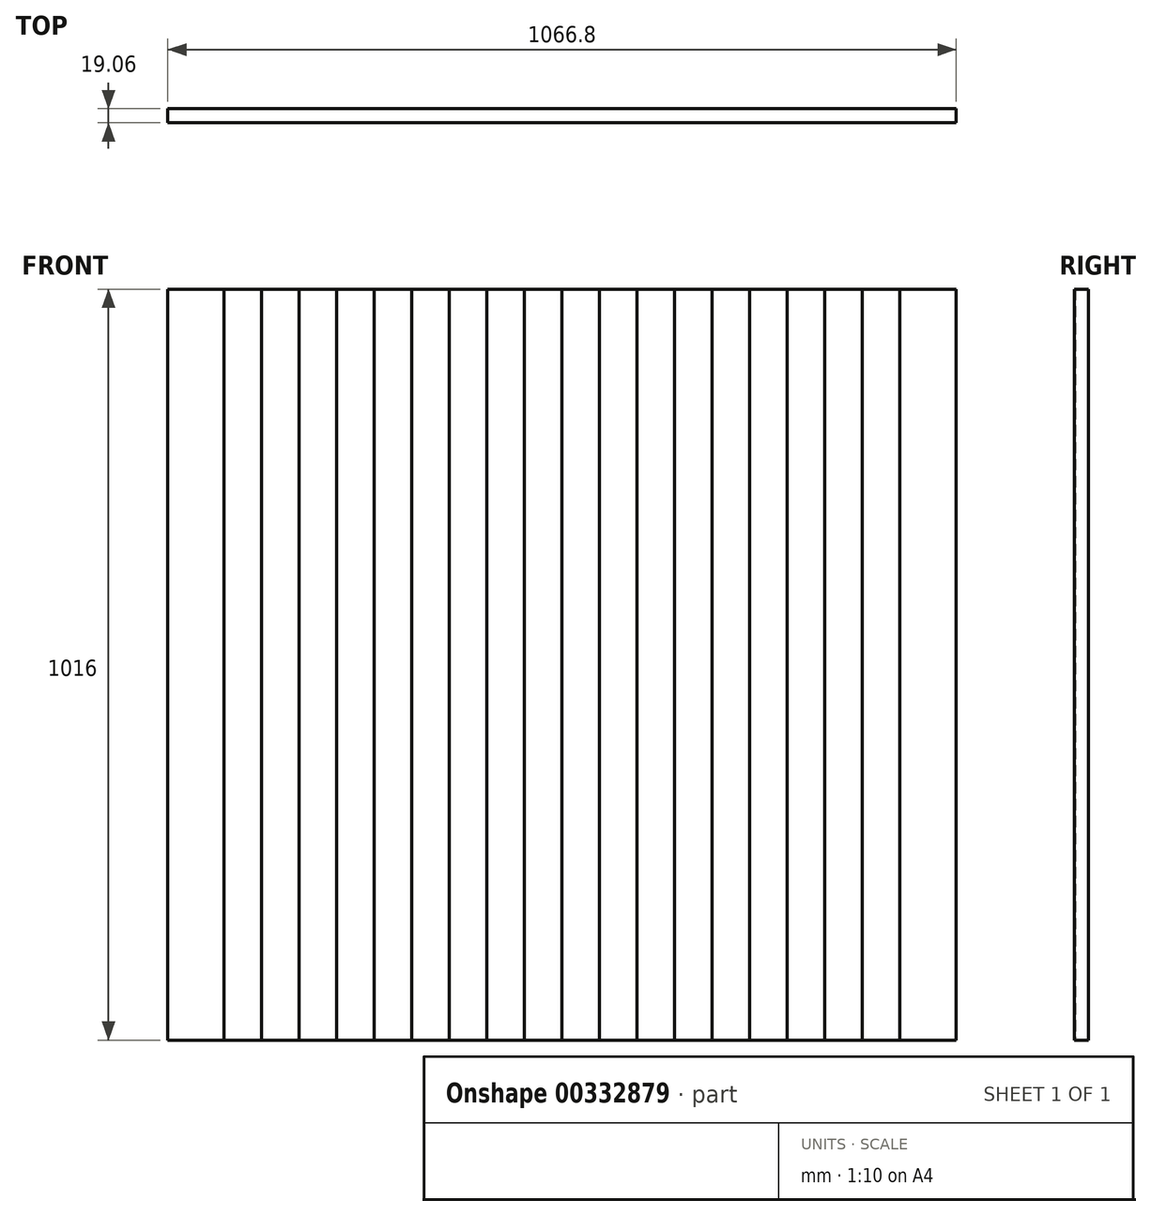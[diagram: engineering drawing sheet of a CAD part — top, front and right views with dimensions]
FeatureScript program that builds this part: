
annotation { "Feature Type Name" : "Feature", "Feature Type Description" : "" }
export const myFeature = defineFeature(function(context is Context, id is Id, definition is map)
    precondition{}
    {
        {
            var Q0;
            Q0=qCreatedBy(makeId("Top.planeOp"),FACE);
            var sketch = newSketch(context, id + "F0", { "sketchPlane" : qUnion([Q0])});
            skLineSegment(sketch, "E0.bottom", {"start": v(533.4, -9.53) * mm, "end": v(458.22, -9.53) * mm});
            skLineSegment(sketch, "E0.top", {"start": v(533.4, 9.53) * mm, "end": v(-533.4, 9.53) * mm});
            skLineSegment(sketch, "E0.left", {"start": v(533.4, 9.53) * mm, "end": v(533.4, -9.53) * mm});
            skLineSegment(sketch, "E0.right", {"start": v(-533.4, 9.53) * mm, "end": v(-533.4, -9.53) * mm});
            skPoint(sketch, "E0.middle", {"position": v(0, 0) * mm});
            skArc(sketch, "E1", {"start": v(-509.02, -9.53) * mm, "mid": v(-508.3, -9.23) * mm, "end": v(-508, -8.5) * mm});
            skArc(sketch, "E2", {"start": v(-508, -8.5) * mm, "mid": v(-507.7, -9.23) * mm, "end": v(-506.98, -9.52) * mm});
            skArc(sketch, "E3.1.0.0", {"start": v(-458.22, -9.53) * mm, "mid": v(-457.5, -9.23) * mm, "end": v(-457.2, -8.5) * mm});
            skArc(sketch, "E3.1.0.1", {"start": v(-457.2, -8.5) * mm, "mid": v(-456.9, -9.23) * mm, "end": v(-456.18, -9.52) * mm});
            skArc(sketch, "E3.2.0.0", {"start": v(-407.42, -9.53) * mm, "mid": v(-406.7, -9.23) * mm, "end": v(-406.4, -8.5) * mm});
            skArc(sketch, "E3.2.0.1", {"start": v(-406.4, -8.5) * mm, "mid": v(-406.1, -9.23) * mm, "end": v(-405.38, -9.52) * mm});
            skArc(sketch, "E3.3.0.0", {"start": v(-356.62, -9.53) * mm, "mid": v(-355.9, -9.23) * mm, "end": v(-355.6, -8.5) * mm});
            skArc(sketch, "E3.3.0.1", {"start": v(-355.6, -8.5) * mm, "mid": v(-355.3, -9.23) * mm, "end": v(-354.58, -9.52) * mm});
            skArc(sketch, "E3.4.0.0", {"start": v(-305.82, -9.53) * mm, "mid": v(-305.1, -9.23) * mm, "end": v(-304.8, -8.5) * mm});
            skArc(sketch, "E3.4.0.1", {"start": v(-304.8, -8.5) * mm, "mid": v(-304.5, -9.23) * mm, "end": v(-303.78, -9.52) * mm});
            skArc(sketch, "E3.5.0.0", {"start": v(-255.02, -9.53) * mm, "mid": v(-254.3, -9.23) * mm, "end": v(-254, -8.5) * mm});
            skArc(sketch, "E3.5.0.1", {"start": v(-254, -8.5) * mm, "mid": v(-253.7, -9.23) * mm, "end": v(-252.98, -9.52) * mm});
            skArc(sketch, "E3.6.0.0", {"start": v(-204.22, -9.53) * mm, "mid": v(-203.5, -9.23) * mm, "end": v(-203.2, -8.5) * mm});
            skArc(sketch, "E3.6.0.1", {"start": v(-203.2, -8.5) * mm, "mid": v(-202.9, -9.23) * mm, "end": v(-202.18, -9.52) * mm});
            skArc(sketch, "E3.7.0.0", {"start": v(-153.42, -9.53) * mm, "mid": v(-152.7, -9.23) * mm, "end": v(-152.4, -8.5) * mm});
            skArc(sketch, "E3.7.0.1", {"start": v(-152.4, -8.5) * mm, "mid": v(-152.1, -9.23) * mm, "end": v(-151.38, -9.52) * mm});
            skArc(sketch, "E3.8.0.0", {"start": v(-102.62, -9.53) * mm, "mid": v(-101.9, -9.23) * mm, "end": v(-101.6, -8.5) * mm});
            skArc(sketch, "E3.8.0.1", {"start": v(-101.6, -8.5) * mm, "mid": v(-101.3, -9.23) * mm, "end": v(-100.58, -9.52) * mm});
            skArc(sketch, "E3.9.0.0", {"start": v(-51.82, -9.53) * mm, "mid": v(-51.1, -9.23) * mm, "end": v(-50.8, -8.5) * mm});
            skArc(sketch, "E3.9.0.1", {"start": v(-50.8, -8.5) * mm, "mid": v(-50.5, -9.23) * mm, "end": v(-49.78, -9.52) * mm});
            skArc(sketch, "E3.10.0.0", {"start": v(-1.02, -9.53) * mm, "mid": v(-0.3, -9.23) * mm, "end": v(0, -8.5) * mm});
            skArc(sketch, "E3.10.0.1", {"start": v(0, -8.5) * mm, "mid": v(0.3, -9.23) * mm, "end": v(1.02, -9.52) * mm});
            skArc(sketch, "E3.11.0.0", {"start": v(49.78, -9.53) * mm, "mid": v(50.5, -9.23) * mm, "end": v(50.8, -8.5) * mm});
            skArc(sketch, "E3.11.0.1", {"start": v(50.8, -8.5) * mm, "mid": v(51.1, -9.23) * mm, "end": v(51.82, -9.52) * mm});
            skArc(sketch, "E3.12.0.0", {"start": v(100.58, -9.53) * mm, "mid": v(101.3, -9.23) * mm, "end": v(101.6, -8.5) * mm});
            skArc(sketch, "E3.12.0.1", {"start": v(101.6, -8.5) * mm, "mid": v(101.9, -9.23) * mm, "end": v(102.62, -9.52) * mm});
            skArc(sketch, "E3.13.0.0", {"start": v(151.38, -9.53) * mm, "mid": v(152.1, -9.23) * mm, "end": v(152.4, -8.5) * mm});
            skArc(sketch, "E3.13.0.1", {"start": v(152.4, -8.5) * mm, "mid": v(152.7, -9.23) * mm, "end": v(153.42, -9.52) * mm});
            skArc(sketch, "E3.14.0.0", {"start": v(202.18, -9.53) * mm, "mid": v(202.9, -9.23) * mm, "end": v(203.2, -8.5) * mm});
            skArc(sketch, "E3.14.0.1", {"start": v(203.2, -8.5) * mm, "mid": v(203.5, -9.23) * mm, "end": v(204.22, -9.52) * mm});
            skArc(sketch, "E3.15.0.0", {"start": v(252.98, -9.53) * mm, "mid": v(253.7, -9.23) * mm, "end": v(254, -8.5) * mm});
            skArc(sketch, "E3.15.0.1", {"start": v(254, -8.5) * mm, "mid": v(254.3, -9.23) * mm, "end": v(255.02, -9.52) * mm});
            skArc(sketch, "E3.16.0.0", {"start": v(303.78, -9.53) * mm, "mid": v(304.5, -9.23) * mm, "end": v(304.8, -8.5) * mm});
            skArc(sketch, "E3.16.0.1", {"start": v(304.8, -8.5) * mm, "mid": v(305.1, -9.23) * mm, "end": v(305.82, -9.52) * mm});
            skArc(sketch, "E3.17.0.0", {"start": v(354.58, -9.53) * mm, "mid": v(355.3, -9.23) * mm, "end": v(355.6, -8.5) * mm});
            skArc(sketch, "E3.17.0.1", {"start": v(355.6, -8.5) * mm, "mid": v(355.9, -9.23) * mm, "end": v(356.62, -9.52) * mm});
            skArc(sketch, "E3.18.0.0", {"start": v(405.38, -9.53) * mm, "mid": v(406.1, -9.23) * mm, "end": v(406.4, -8.5) * mm});
            skArc(sketch, "E3.18.0.1", {"start": v(406.4, -8.5) * mm, "mid": v(406.7, -9.23) * mm, "end": v(407.42, -9.52) * mm});
            skArc(sketch, "E3.19.0.0", {"start": v(456.18, -9.53) * mm, "mid": v(456.9, -9.23) * mm, "end": v(457.2, -8.5) * mm});
            skArc(sketch, "E3.19.0.1", {"start": v(457.2, -8.5) * mm, "mid": v(457.5, -9.23) * mm, "end": v(458.22, -9.52) * mm});
            skLineSegment(sketch, "E3.direction1", {"start": v(-506.98, -9.53) * mm, "end": v(-458.22, -9.53) * mm, "construction": true});
            skLineSegment(sketch, "E4.trimOffspring", {"start": v(-458.22, -9.53) * mm, "end": v(-533.4, -9.53) * mm});
            skLineSegment(sketch, "E5.trimOffspring", {"start": v(-407.42, -9.53) * mm, "end": v(-456.18, -9.53) * mm});
            skLineSegment(sketch, "E6.trimOffspring", {"start": v(-356.62, -9.53) * mm, "end": v(-405.38, -9.53) * mm});
            skLineSegment(sketch, "E7.trimOffspring", {"start": v(-305.82, -9.53) * mm, "end": v(-354.58, -9.53) * mm});
            skLineSegment(sketch, "E8.trimOffspring", {"start": v(-255.02, -9.53) * mm, "end": v(-303.78, -9.53) * mm});
            skLineSegment(sketch, "E9.trimOffspring", {"start": v(-204.22, -9.53) * mm, "end": v(-252.98, -9.53) * mm});
            skLineSegment(sketch, "E10.trimOffspring", {"start": v(-153.42, -9.53) * mm, "end": v(-202.18, -9.53) * mm});
            skLineSegment(sketch, "E11.trimOffspring", {"start": v(-102.62, -9.53) * mm, "end": v(-151.38, -9.53) * mm});
            skLineSegment(sketch, "E12.trimOffspring", {"start": v(-51.82, -9.53) * mm, "end": v(-100.58, -9.53) * mm});
            skLineSegment(sketch, "E13.trimOffspring", {"start": v(-1.02, -9.53) * mm, "end": v(-49.78, -9.53) * mm});
            skLineSegment(sketch, "E14.trimOffspring", {"start": v(49.78, -9.53) * mm, "end": v(1.02, -9.53) * mm});
            skLineSegment(sketch, "E15.trimOffspring", {"start": v(100.58, -9.53) * mm, "end": v(51.82, -9.53) * mm});
            skLineSegment(sketch, "E16.trimOffspring", {"start": v(151.38, -9.53) * mm, "end": v(102.62, -9.53) * mm});
            skLineSegment(sketch, "E17.trimOffspring", {"start": v(202.18, -9.53) * mm, "end": v(153.42, -9.53) * mm});
            skLineSegment(sketch, "E18.trimOffspring", {"start": v(252.98, -9.53) * mm, "end": v(204.22, -9.53) * mm});
            skLineSegment(sketch, "E19.trimOffspring", {"start": v(303.78, -9.53) * mm, "end": v(255.02, -9.53) * mm});
            skLineSegment(sketch, "E20.trimOffspring", {"start": v(354.58, -9.53) * mm, "end": v(305.82, -9.53) * mm});
            skLineSegment(sketch, "E21.trimOffspring", {"start": v(405.38, -9.53) * mm, "end": v(356.62, -9.53) * mm});
            skLineSegment(sketch, "E22.trimOffspring", {"start": v(456.18, -9.53) * mm, "end": v(407.42, -9.53) * mm});
            skArc(sketch, "E23.0.20.0", {"start": v(506.98, -9.53) * mm, "mid": v(507.7, -9.23) * mm, "end": v(508, -8.5) * mm});
            skArc(sketch, "E23.4.20.0", {"start": v(508, -8.5) * mm, "mid": v(508.3, -9.23) * mm, "end": v(509.02, -9.52) * mm});
            skArc(sketch, "E23.0.21.0", {"start": v(557.78, -9.53) * mm, "mid": v(558.5, -9.23) * mm, "end": v(558.8, -8.5) * mm});
            skArc(sketch, "E23.4.21.0", {"start": v(558.8, -8.5) * mm, "mid": v(559.1, -9.23) * mm, "end": v(559.82, -9.52) * mm});
            skArc(sketch, "E23.0.22.0", {"start": v(608.58, -9.53) * mm, "mid": v(609.3, -9.23) * mm, "end": v(609.6, -8.5) * mm});
            skArc(sketch, "E23.4.22.0", {"start": v(609.6, -8.5) * mm, "mid": v(609.9, -9.23) * mm, "end": v(610.62, -9.52) * mm});
            skArc(sketch, "E23.0.23.0", {"start": v(659.38, -9.53) * mm, "mid": v(660.1, -9.23) * mm, "end": v(660.4, -8.5) * mm});
            skArc(sketch, "E23.4.23.0", {"start": v(660.4, -8.5) * mm, "mid": v(660.7, -9.23) * mm, "end": v(661.42, -9.52) * mm});
            skArc(sketch, "E23.0.24.0", {"start": v(710.18, -9.53) * mm, "mid": v(710.9, -9.23) * mm, "end": v(711.2, -8.5) * mm});
            skArc(sketch, "E23.4.24.0", {"start": v(711.2, -8.5) * mm, "mid": v(711.5, -9.23) * mm, "end": v(712.22, -9.52) * mm});
            skArc(sketch, "E23.0.25.0", {"start": v(760.98, -9.53) * mm, "mid": v(761.7, -9.23) * mm, "end": v(762, -8.5) * mm});
            skArc(sketch, "E23.4.25.0", {"start": v(762, -8.5) * mm, "mid": v(762.3, -9.23) * mm, "end": v(763.02, -9.52) * mm});
            skArc(sketch, "E23.0.26.0", {"start": v(811.78, -9.53) * mm, "mid": v(812.5, -9.23) * mm, "end": v(812.8, -8.5) * mm});
            skArc(sketch, "E23.4.26.0", {"start": v(812.8, -8.5) * mm, "mid": v(813.1, -9.23) * mm, "end": v(813.82, -9.52) * mm});
            skArc(sketch, "E23.0.27.0", {"start": v(862.58, -9.53) * mm, "mid": v(863.3, -9.23) * mm, "end": v(863.6, -8.5) * mm});
            skArc(sketch, "E23.4.27.0", {"start": v(863.6, -8.5) * mm, "mid": v(863.9, -9.23) * mm, "end": v(864.62, -9.52) * mm});
            skArc(sketch, "E23.0.28.0", {"start": v(913.38, -9.53) * mm, "mid": v(914.1, -9.23) * mm, "end": v(914.4, -8.5) * mm});
            skArc(sketch, "E23.4.28.0", {"start": v(914.4, -8.5) * mm, "mid": v(914.7, -9.23) * mm, "end": v(915.42, -9.52) * mm});
            skArc(sketch, "E23.0.29.0", {"start": v(964.18, -9.53) * mm, "mid": v(964.9, -9.23) * mm, "end": v(965.2, -8.5) * mm});
            skArc(sketch, "E23.4.29.0", {"start": v(965.2, -8.5) * mm, "mid": v(965.5, -9.23) * mm, "end": v(966.22, -9.52) * mm});
            skArc(sketch, "E23.0.30.0", {"start": v(1014.98, -9.53) * mm, "mid": v(1015.7, -9.23) * mm, "end": v(1016, -8.5) * mm});
            skArc(sketch, "E23.4.30.0", {"start": v(1016, -8.5) * mm, "mid": v(1016.3, -9.23) * mm, "end": v(1017.02, -9.52) * mm});
            skArc(sketch, "E23.0.31.0", {"start": v(1065.78, -9.53) * mm, "mid": v(1066.5, -9.23) * mm, "end": v(1066.8, -8.5) * mm});
            skArc(sketch, "E23.4.31.0", {"start": v(1066.8, -8.5) * mm, "mid": v(1067.1, -9.23) * mm, "end": v(1067.82, -9.52) * mm});
            skArc(sketch, "E23.0.32.0", {"start": v(1116.58, -9.53) * mm, "mid": v(1117.3, -9.23) * mm, "end": v(1117.6, -8.5) * mm});
            skArc(sketch, "E23.4.32.0", {"start": v(1117.6, -8.5) * mm, "mid": v(1117.9, -9.23) * mm, "end": v(1118.62, -9.52) * mm});
            skArc(sketch, "E23.0.33.0", {"start": v(1167.38, -9.53) * mm, "mid": v(1168.1, -9.23) * mm, "end": v(1168.4, -8.5) * mm});
            skArc(sketch, "E23.4.33.0", {"start": v(1168.4, -8.5) * mm, "mid": v(1168.7, -9.23) * mm, "end": v(1169.42, -9.52) * mm});
            skArc(sketch, "E23.0.34.0", {"start": v(1218.18, -9.53) * mm, "mid": v(1218.9, -9.23) * mm, "end": v(1219.2, -8.5) * mm});
            skArc(sketch, "E23.4.34.0", {"start": v(1219.2, -8.5) * mm, "mid": v(1219.5, -9.23) * mm, "end": v(1220.22, -9.52) * mm});
            skArc(sketch, "E23.0.35.0", {"start": v(1268.98, -9.53) * mm, "mid": v(1269.7, -9.23) * mm, "end": v(1270, -8.5) * mm});
            skArc(sketch, "E23.4.35.0", {"start": v(1270, -8.5) * mm, "mid": v(1270.3, -9.23) * mm, "end": v(1271.02, -9.52) * mm});
            skArc(sketch, "E23.0.36.0", {"start": v(1319.78, -9.53) * mm, "mid": v(1320.5, -9.23) * mm, "end": v(1320.8, -8.5) * mm});
            skArc(sketch, "E23.4.36.0", {"start": v(1320.8, -8.5) * mm, "mid": v(1321.1, -9.23) * mm, "end": v(1321.82, -9.52) * mm});
            skArc(sketch, "E23.0.37.0", {"start": v(1370.58, -9.53) * mm, "mid": v(1371.3, -9.23) * mm, "end": v(1371.6, -8.5) * mm});
            skArc(sketch, "E23.4.37.0", {"start": v(1371.6, -8.5) * mm, "mid": v(1371.9, -9.23) * mm, "end": v(1372.62, -9.52) * mm});
            skArc(sketch, "E23.0.38.0", {"start": v(1421.38, -9.53) * mm, "mid": v(1422.1, -9.23) * mm, "end": v(1422.4, -8.5) * mm});
            skArc(sketch, "E23.4.38.0", {"start": v(1422.4, -8.5) * mm, "mid": v(1422.7, -9.23) * mm, "end": v(1423.42, -9.52) * mm});
            skArc(sketch, "E23.0.39.0", {"start": v(1472.18, -9.53) * mm, "mid": v(1472.9, -9.23) * mm, "end": v(1473.2, -8.5) * mm});
            skArc(sketch, "E23.4.39.0", {"start": v(1473.2, -8.5) * mm, "mid": v(1473.5, -9.23) * mm, "end": v(1474.22, -9.52) * mm});
            skSolve(sketch);
        }
        {
            var Q0;
            Q0 = qSketchRegion(id + "F0", true);
            extrude(context, id + "F1", {"entities" : qUnion([Q0]), "depth" : 1016 * mm});
        }
    });
